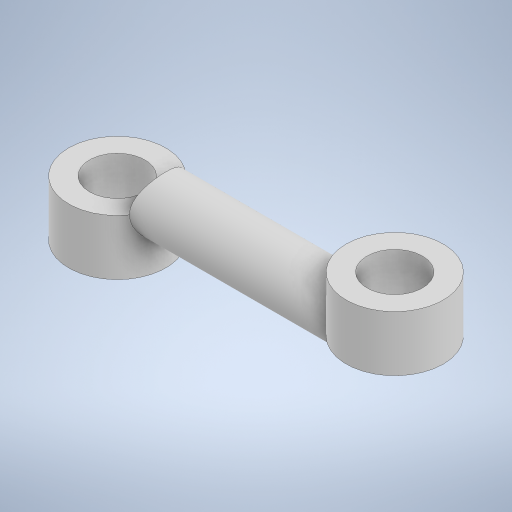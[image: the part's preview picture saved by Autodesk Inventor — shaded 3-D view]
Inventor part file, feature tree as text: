
AUTODESK INVENTOR PART (.ipt)
format: ipt  version: 2024 (Build 280153000, 153)  size: 278,016 bytes
history: native  units: in
note: dims shown in document units (in); Inventor stores cm internally (conversion verified against a paired STEP export)
features: extrude x6, sketch x3, revolve x1
ambient origin geometry x8: Origin, YZ Plane, XZ Plane, XY Plane, X Axis, Y Axis, Z Axis, Center Point
bodies: Solid1 (feature_tree)
feature tree (10):
  revolve  "Revolution1"  [1 undecoded]
  sketch  "Sketch2"  dims[d2=90.0deg d3=1.378in]
  extrude  "Extrusion1"  Depth=1.378in
  extrude  "Extrusion2"  Depth=0.7874in TaperAngle=0.0deg
  extrude  "Extrusion3"  Depth=0.7874in TaperAngle=0.0deg
  sketch  "Sketch4"  dims[d4=0.7874in d5=0.7874in d6=0.0in d7=0.7874in d8=0.0in d9=0.7874in d10=0.0in d17=1.378in d18=0.7874in d19=0.7874in d20=0.0in d21=0.7874in d22=0.0in d23=0.7874in d24=0.0in]
  extrude  "Extrusion6"  Depth=0.7874in TaperAngle=0.0deg
  extrude  "Extrusion7"  Depth=1.378in
  extrude  "Extrusion8"  Depth=0.7874in
  sketch  "Sketch1"  dims[d0=3.937in d1=0.3937in]
note: 1 required parameter value undecoded (feature->parameter linkage not recoverable at this tier; creation-order binding heuristic only, values carry confidence <= 0.55)
